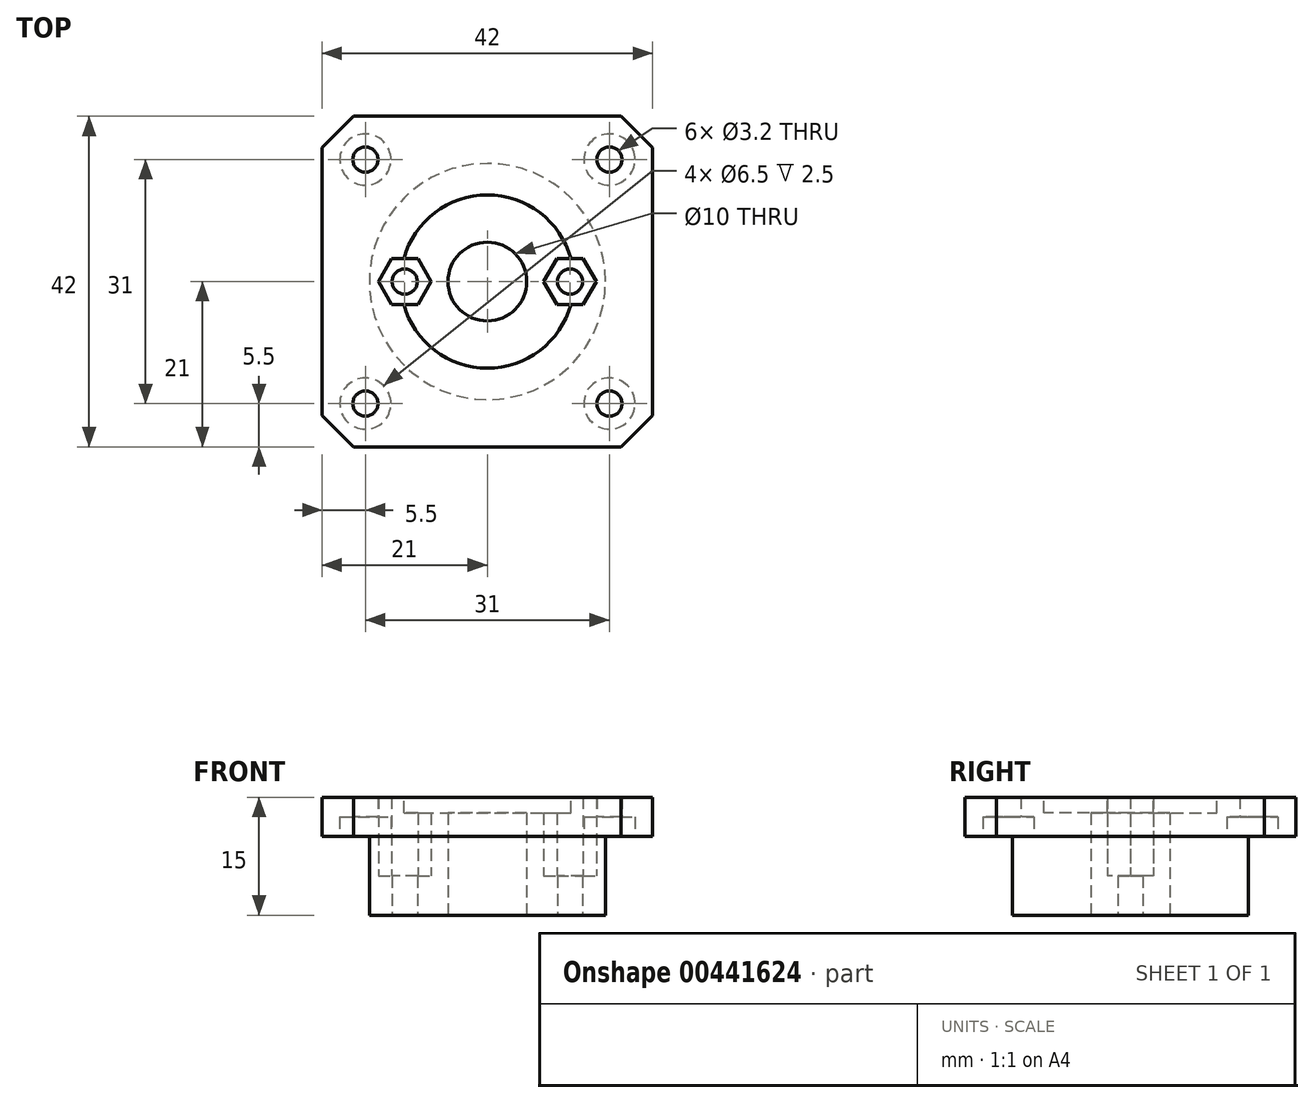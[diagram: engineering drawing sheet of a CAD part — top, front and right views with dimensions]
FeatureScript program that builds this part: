
annotation { "Feature Type Name" : "Feature", "Feature Type Description" : "" }
export const myFeature = defineFeature(function(context is Context, id is Id, definition is map)
    precondition{}
    {
        {
            var Q0;
            Q0=qCreatedBy(makeId("Top.planeOp"),FACE);
            var sketch = newSketch(context, id + "F0", { "sketchPlane" : qUnion([Q0])});
            skCircle(sketch, "E0", {"center": v(0, 0) * mm, "radius": 15 * mm});
            skCircle(sketch, "E1", {"center": v(0, 0) * mm, "radius": 5 * mm});
            skCircle(sketch, "E2", {"center": v(-10.5, 0) * mm, "radius": 1.6 * mm});
            skCircle(sketch, "E3", {"center": v(10.5, 0) * mm, "radius": 1.6 * mm});
            skLineSegment(sketch, "E4", {"start": v(-10.5, 0) * mm, "end": v(0, 0) * mm, "construction": true});
            skLineSegment(sketch, "E5", {"start": v(10.5, 0) * mm, "end": v(0, 0) * mm, "construction": true});
            skSolve(sketch);
        }
        {
            var Q0;
            Q0=makeQuery(id+"F0.imprint","IMPRINT",FACE,{"disambiguationData":[TD([[makeQuery(id+"F0.imprint","IMPRINT",EDGE,{"derivedFrom":sQuery(id+"F0.wireOp",EDGE,"E0")}),1.0]])]});
            extrude(context, id + "F1", {"entities" : qUnion([Q0]), "depth" : 5 * mm});
        }
        {
            var Q0;
            Q0=makeQuery(id+"F1.opExtrude","CAP_FACE",FACE,{"disambiguationData":[OSD([sQuery(id+"F0.wireOp",EDGE,"E0"),sQuery(id+"F0.wireOp",EDGE,"E1"),sQuery(id+"F0.wireOp",EDGE,"E2"),sQuery(id+"F0.wireOp",EDGE,"E3")])],"isStart":false});
            var sketch = newSketch(context, id + "F2", { "sketchPlane" : qUnion([Q0])});
            skLineSegment(sketch, "E6.bottom", {"start": v(-21, 21) * mm, "end": v(21, 21) * mm});
            skLineSegment(sketch, "E6.top", {"start": v(-21, -21) * mm, "end": v(21, -21) * mm});
            skLineSegment(sketch, "E6.left", {"start": v(-21, 21) * mm, "end": v(-21, -21) * mm});
            skLineSegment(sketch, "E6.right", {"start": v(21, 21) * mm, "end": v(21, -21) * mm});
            skLineSegment(sketch, "E7", {"start": v(0, 21) * mm, "end": v(0, 0) * mm, "construction": true});
            skLineSegment(sketch, "E8", {"start": v(0, 0) * mm, "end": v(-21, 0) * mm, "construction": true});
            skCircle(sketch, "E9", {"center": v(-15.5, 15.5) * mm, "radius": 1.6 * mm});
            skCircle(sketch, "E10", {"center": v(15.5, 15.5) * mm, "radius": 1.6 * mm});
            skCircle(sketch, "E11", {"center": v(15.5, -15.5) * mm, "radius": 1.6 * mm});
            skCircle(sketch, "E12", {"center": v(-15.5, -15.5) * mm, "radius": 1.6 * mm});
            skLineSegment(sketch, "E13", {"start": v(-15.5, 15.5) * mm, "end": v(-15.5, -15.5) * mm, "construction": true});
            skLineSegment(sketch, "E14", {"start": v(-15.5, 0) * mm, "end": v(0, 0) * mm, "construction": true});
            skLineSegment(sketch, "E15", {"start": v(-15.5, 15.5) * mm, "end": v(15.5, 15.5) * mm, "construction": true});
            skLineSegment(sketch, "E16", {"start": v(0, 15.5) * mm, "end": v(0, 0) * mm, "construction": true});
            skLineSegment(sketch, "E17", {"start": v(-12.17, 2.9) * mm, "end": v(-8.83, 2.9) * mm});
            skLineSegment(sketch, "E18", {"start": v(-8.83, 2.9) * mm, "end": v(-7.15, 0) * mm});
            skLineSegment(sketch, "E19", {"start": v(-7.15, 0) * mm, "end": v(-8.83, -2.9) * mm});
            skLineSegment(sketch, "E20", {"start": v(-8.83, -2.9) * mm, "end": v(-12.17, -2.9) * mm});
            skLineSegment(sketch, "E21", {"start": v(-12.17, -2.9) * mm, "end": v(-13.85, 0) * mm});
            skLineSegment(sketch, "E22", {"start": v(-13.85, 0) * mm, "end": v(-12.17, 2.9) * mm});
            skCircle(sketch, "E23.0", {"center": v(-10.5, 0) * mm, "radius": 1.6 * mm});
            skCircle(sketch, "E24.0", {"center": v(10.5, 0) * mm, "radius": 1.6 * mm});
            skLineSegment(sketch, "E25", {"start": v(-10.5, 2.9) * mm, "end": v(-10.5, 0) * mm, "construction": true});
            skLineSegment(sketch, "E26", {"start": v(-13.01, -1.45) * mm, "end": v(-10.5, 0) * mm, "construction": true});
            skLineSegment(sketch, "E27.MirrorCS", {"start": v(13.01, -1.45) * mm, "end": v(10.5, 0) * mm, "construction": true});
            skLineSegment(sketch, "E28.MirrorCS", {"start": v(10.5, 2.9) * mm, "end": v(10.5, 0) * mm, "construction": true});
            skLineSegment(sketch, "E29.MirrorCS", {"start": v(12.17, -2.9) * mm, "end": v(13.85, 0) * mm});
            skLineSegment(sketch, "E30.MirrorCS", {"start": v(8.83, -2.9) * mm, "end": v(12.17, -2.9) * mm});
            skLineSegment(sketch, "E31.MirrorCS", {"start": v(7.15, 0) * mm, "end": v(8.83, -2.9) * mm});
            skLineSegment(sketch, "E32.MirrorCS", {"start": v(8.83, 2.9) * mm, "end": v(7.15, 0) * mm});
            skLineSegment(sketch, "E33.MirrorCS", {"start": v(12.17, 2.9) * mm, "end": v(8.83, 2.9) * mm});
            skLineSegment(sketch, "E34.MirrorCS", {"start": v(13.85, 0) * mm, "end": v(12.17, 2.9) * mm});
            skSolve(sketch);
        }
        {
            var Q0;
            Q0=makeQuery(id+"F2.imprint","IMPRINT",FACE,{"disambiguationData":[TD([[makeQuery(id+"F2.imprint","IMPRINT",EDGE,{"derivedFrom":sQuery(id+"F2.wireOp",EDGE,"E6.bottom")}),-1.0]])]});
            var Q1;
            Q1=makeQuery(id+"F2.imprint","IMPRINT",FACE,{"disambiguationData":[TD([[makeQuery(id+"F2.imprint","IMPRINT",EDGE,{"derivedFrom":sQuery(id+"F2.wireOp",EDGE,"E17")}),1.0]])]});
            extrude(context, id + "F3", {"entities" : qUnion([Q0, Q1]), "operationType" : NewBodyOperationType.ADD, "depth" : 5 * mm});
        }
        {
            var Q0;
            Q0=makeQuery(id+"F3.opExtrude","SWEPT_EDGE",EDGE,{"disambiguationData":[OSD([sQuery(id+"F2.wireOp",EDGE,"E6.bottom"),sQuery(id+"F2.wireOp",EDGE,"E6.right")])]});
            var Q1;
            Q1=makeQuery(id+"F3.opExtrude","SWEPT_EDGE",EDGE,{"disambiguationData":[OSD([sQuery(id+"F2.wireOp",EDGE,"E6.top"),sQuery(id+"F2.wireOp",EDGE,"E6.right")])]});
            var Q2;
            Q2=makeQuery(id+"F3.opExtrude","SWEPT_EDGE",EDGE,{"disambiguationData":[OSD([sQuery(id+"F2.wireOp",EDGE,"E6.top"),sQuery(id+"F2.wireOp",EDGE,"E6.left")])]});
            var Q3;
            Q3=makeQuery(id+"F3.opExtrude","SWEPT_EDGE",EDGE,{"disambiguationData":[OSD([sQuery(id+"F2.wireOp",EDGE,"E6.bottom"),sQuery(id+"F2.wireOp",EDGE,"E6.left")])]});
            chamfer(context, id + "F4", {"entities" : qUnion([Q0, Q1, Q2, Q3]), "width" : 4 * mm, "tangentPropagation" : true});
        }
        {
            var Q0;
            Q0=makeQuery(id+"F3.opExtrude","CAP_FACE",FACE,{"disambiguationData":[OSD([sQuery(id+"F0.wireOp",EDGE,"E1"),sQuery(id+"F2.wireOp",EDGE,"E6.bottom"),sQuery(id+"F2.wireOp",EDGE,"E6.top"),sQuery(id+"F2.wireOp",EDGE,"E6.left"),sQuery(id+"F2.wireOp",EDGE,"E6.right"),sQuery(id+"F2.wireOp",EDGE,"E9"),sQuery(id+"F2.wireOp",EDGE,"E10"),sQuery(id+"F2.wireOp",EDGE,"E11"),sQuery(id+"F2.wireOp",EDGE,"E12"),sQuery(id+"F2.wireOp",EDGE,"E17"),sQuery(id+"F2.wireOp",EDGE,"E18"),sQuery(id+"F2.wireOp",EDGE,"E19"),sQuery(id+"F2.wireOp",EDGE,"E20"),sQuery(id+"F2.wireOp",EDGE,"E21"),sQuery(id+"F2.wireOp",EDGE,"E22"),sQuery(id+"F2.wireOp",EDGE,"E29.MirrorCS"),sQuery(id+"F2.wireOp",EDGE,"E30.MirrorCS"),sQuery(id+"F2.wireOp",EDGE,"E31.MirrorCS"),sQuery(id+"F2.wireOp",EDGE,"E32.MirrorCS"),sQuery(id+"F2.wireOp",EDGE,"E33.MirrorCS"),sQuery(id+"F2.wireOp",EDGE,"E34.MirrorCS")])],"isStart":false});
            var sketch = newSketch(context, id + "F5", { "sketchPlane" : qUnion([Q0])});
            skCircle(sketch, "E35.0", {"center": v(0, 0) * mm, "radius": 5 * mm});
            skCircle(sketch, "E36", {"center": v(0, 0) * mm, "radius": 11 * mm});
            skSolve(sketch);
        }
        {
            var Q0;
            Q0=makeQuery(id+"F5.imprint","IMPRINT",FACE,{"disambiguationData":[TD([[makeQuery(id+"F5.imprint","IMPRINT",EDGE,{"derivedFrom":sQuery(id+"F5.wireOp",EDGE,"E35.0")}),-1.0]])]});
            extrude(context, id + "F6", {"entities" : qUnion([Q0]), "operationType" : NewBodyOperationType.REMOVE, "oppositeDirection" : true, "depth" : 2 * mm});
        }
        {
            var Q0;
            Q0=makeQuery(id+"F1.opExtrude","CAP_FACE",FACE,{"disambiguationData":[OSD([sQuery(id+"F0.wireOp",EDGE,"E0"),sQuery(id+"F0.wireOp",EDGE,"E1"),sQuery(id+"F0.wireOp",EDGE,"E2"),sQuery(id+"F0.wireOp",EDGE,"E3")])],"isStart":true});
            var sketch = newSketch(context, id + "F7", { "sketchPlane" : qUnion([Q0])});
            skCircle(sketch, "E37.0.0", {"center": v(0, 0) * mm, "radius": 15 * mm});
            skSolve(sketch);
        }
        {
            var Q0;
            Q0=makeQuery(id+"F7.imprint","IMPRINT",FACE,{"disambiguationData":[TD([[makeQuery(id+"F7.imprint","IMPRINT",EDGE,{"derivedFrom":sQuery(id+"F7.wireOp",EDGE,"E37.0.0")}),-1.0]])]});
            extrude(context, id + "F8", {"entities" : qUnion([Q0]), "operationType" : NewBodyOperationType.ADD, "depth" : 5 * mm});
        }
        {
            var Q0;
            {var subQ0=sQuery(id+"F0.wireOp",EDGE,"E2");Q0=makeQuery(id+"F3.boolean.opBoolean","SPLIT",FACE,{"disambiguationData":[TD([makeQuery(id+"F1.opExtrude","SWEPT_FACE",FACE,{"disambiguationData":[OSD([subQ0])]})])],"derivedFrom":makeQuery(id+"F1.opExtrude","CAP_FACE",FACE,{"disambiguationData":[OSD([sQuery(id+"F0.wireOp",EDGE,"E0"),sQuery(id+"F0.wireOp",EDGE,"E1"),subQ0,sQuery(id+"F0.wireOp",EDGE,"E3")])],"isStart":false})});}
            var sketch = newSketch(context, id + "F9", { "sketchPlane" : qUnion([Q0])});
            skLineSegment(sketch, "E38.0.0", {"start": v(-13.85, 0) * mm, "end": v(-12.17, -2.9) * mm});
            skLineSegment(sketch, "E38.0.1", {"start": v(-12.17, -2.9) * mm, "end": v(-8.83, -2.9) * mm});
            skLineSegment(sketch, "E38.0.2", {"start": v(-8.83, -2.9) * mm, "end": v(-7.15, 0) * mm});
            skLineSegment(sketch, "E38.0.3", {"start": v(-7.15, 0) * mm, "end": v(-8.83, 2.9) * mm});
            skLineSegment(sketch, "E38.0.4", {"start": v(-8.83, 2.9) * mm, "end": v(-12.17, 2.9) * mm});
            skLineSegment(sketch, "E38.0.5", {"start": v(-12.17, 2.9) * mm, "end": v(-13.85, 0) * mm});
            skLineSegment(sketch, "E39.0.0", {"start": v(12.17, -2.9) * mm, "end": v(13.85, 0) * mm});
            skLineSegment(sketch, "E39.0.1", {"start": v(13.85, 0) * mm, "end": v(12.17, 2.9) * mm});
            skLineSegment(sketch, "E39.0.2", {"start": v(12.17, 2.9) * mm, "end": v(8.83, 2.9) * mm});
            skLineSegment(sketch, "E39.0.3", {"start": v(8.83, 2.9) * mm, "end": v(7.15, 0) * mm});
            skLineSegment(sketch, "E39.0.4", {"start": v(7.15, 0) * mm, "end": v(8.83, -2.9) * mm});
            skLineSegment(sketch, "E39.0.5", {"start": v(8.83, -2.9) * mm, "end": v(12.17, -2.9) * mm});
            skSolve(sketch);
        }
        {
            var Q0;
            Q0=makeQuery(id+"F9.imprint","IMPRINT",FACE,{"disambiguationData":[TD([[makeQuery(id+"F9.imprint","IMPRINT",EDGE,{"derivedFrom":sQuery(id+"F9.wireOp",EDGE,"E38.0.0")}),-1.0]])]});
            var Q1;
            Q1=makeQuery(id+"F9.imprint","IMPRINT",FACE,{"disambiguationData":[TD([[makeQuery(id+"F9.imprint","IMPRINT",EDGE,{"derivedFrom":sQuery(id+"F9.wireOp",EDGE,"E39.0.0")}),1.0]])]});
            extrude(context, id + "F10", {"entities" : qUnion([Q0, Q1]), "operationType" : NewBodyOperationType.REMOVE, "oppositeDirection" : true, "depth" : 5 * mm});
        }
        {
            var Q0;
            Q0=makeQuery(id+"F3.opExtrude","CAP_FACE",FACE,{"disambiguationData":[OSD([sQuery(id+"F0.wireOp",EDGE,"E1"),sQuery(id+"F2.wireOp",EDGE,"E6.bottom"),sQuery(id+"F2.wireOp",EDGE,"E6.top"),sQuery(id+"F2.wireOp",EDGE,"E6.left"),sQuery(id+"F2.wireOp",EDGE,"E6.right"),sQuery(id+"F2.wireOp",EDGE,"E9"),sQuery(id+"F2.wireOp",EDGE,"E10"),sQuery(id+"F2.wireOp",EDGE,"E11"),sQuery(id+"F2.wireOp",EDGE,"E12"),sQuery(id+"F2.wireOp",EDGE,"E17"),sQuery(id+"F2.wireOp",EDGE,"E18"),sQuery(id+"F2.wireOp",EDGE,"E19"),sQuery(id+"F2.wireOp",EDGE,"E20"),sQuery(id+"F2.wireOp",EDGE,"E21"),sQuery(id+"F2.wireOp",EDGE,"E22"),sQuery(id+"F2.wireOp",EDGE,"E29.MirrorCS"),sQuery(id+"F2.wireOp",EDGE,"E30.MirrorCS"),sQuery(id+"F2.wireOp",EDGE,"E31.MirrorCS"),sQuery(id+"F2.wireOp",EDGE,"E32.MirrorCS"),sQuery(id+"F2.wireOp",EDGE,"E33.MirrorCS"),sQuery(id+"F2.wireOp",EDGE,"E34.MirrorCS")])],"isStart":true});
            var sketch = newSketch(context, id + "F11", { "sketchPlane" : qUnion([Q0])});
            skCircle(sketch, "E40.0", {"center": v(15.5, 15.5) * mm, "radius": 1.6 * mm});
            skCircle(sketch, "E41.0", {"center": v(15.5, -15.5) * mm, "radius": 1.6 * mm});
            skCircle(sketch, "E42.0", {"center": v(-15.5, -15.5) * mm, "radius": 1.6 * mm});
            skCircle(sketch, "E43.0", {"center": v(-15.5, 15.5) * mm, "radius": 1.6 * mm});
            skCircle(sketch, "E44", {"center": v(15.5, 15.5) * mm, "radius": 3.25 * mm});
            skCircle(sketch, "E45", {"center": v(15.5, -15.5) * mm, "radius": 3.25 * mm});
            skCircle(sketch, "E46", {"center": v(-15.5, -15.5) * mm, "radius": 3.25 * mm});
            skCircle(sketch, "E47", {"center": v(-15.5, 15.5) * mm, "radius": 3.25 * mm});
            skSolve(sketch);
        }
        {
            var Q0;
            Q0=makeQuery(id+"F11.imprint","IMPRINT",FACE,{"disambiguationData":[TD([[makeQuery(id+"F11.imprint","IMPRINT",EDGE,{"derivedFrom":sQuery(id+"F11.wireOp",EDGE,"E40.0")}),1.0]])]});
            var Q1;
            Q1=makeQuery(id+"F11.imprint","IMPRINT",FACE,{"disambiguationData":[TD([[makeQuery(id+"F11.imprint","IMPRINT",EDGE,{"derivedFrom":sQuery(id+"F11.wireOp",EDGE,"E41.0")}),1.0]])]});
            var Q2;
            Q2=makeQuery(id+"F11.imprint","IMPRINT",FACE,{"disambiguationData":[TD([[makeQuery(id+"F11.imprint","IMPRINT",EDGE,{"derivedFrom":sQuery(id+"F11.wireOp",EDGE,"E42.0")}),1.0]])]});
            var Q3;
            Q3=makeQuery(id+"F11.imprint","IMPRINT",FACE,{"disambiguationData":[TD([[makeQuery(id+"F11.imprint","IMPRINT",EDGE,{"derivedFrom":sQuery(id+"F11.wireOp",EDGE,"E43.0")}),1.0]])]});
            extrude(context, id + "F12", {"entities" : qUnion([Q0, Q1, Q2, Q3]), "operationType" : NewBodyOperationType.REMOVE, "oppositeDirection" : true, "depth" : 2.5 * mm});
        }
    });
